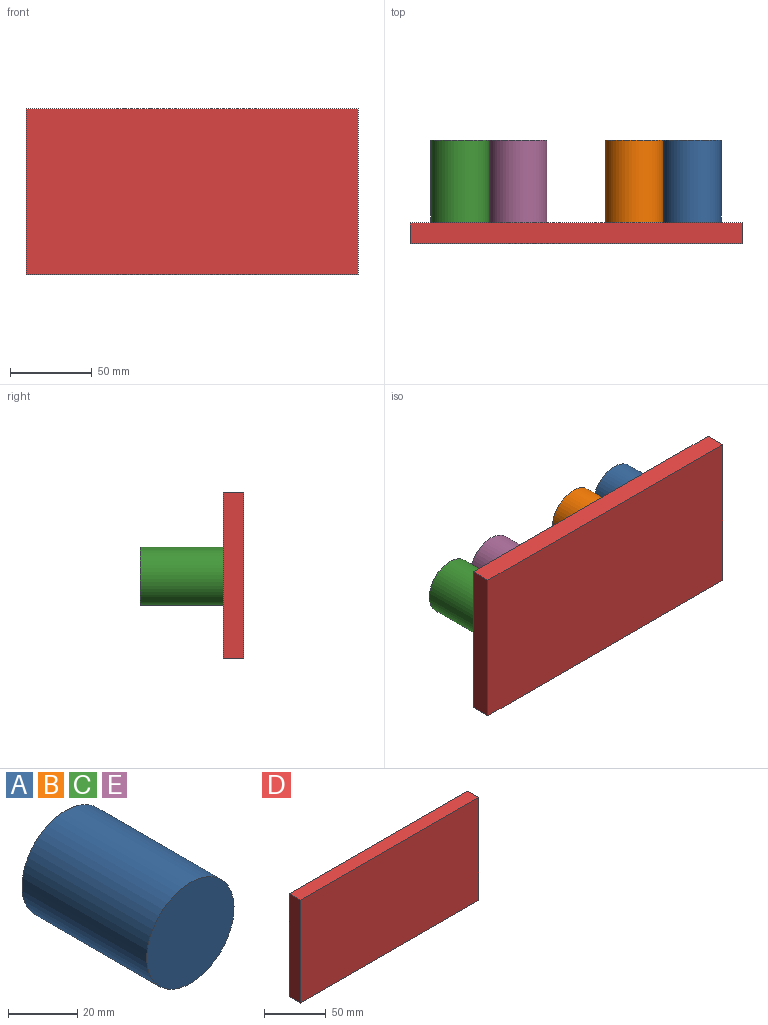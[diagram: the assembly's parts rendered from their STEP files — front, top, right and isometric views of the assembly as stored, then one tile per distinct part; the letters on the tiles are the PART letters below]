
ASSEMBLY  parts=5 mates=4
PART A: 3 faces, bbox 35.6x50.8x35.6 mm
  f0: cylinder r=17.78mm len=50.8mm, axis (0,1,0), area 5675.1mm2, adj f1,f2
  f1: plane 35.56x35.56mm, normal (0,-1,0), area 993.1mm2, adj f0
  f2: plane 35.56x35.56mm, normal (0,1,0), area 993.1mm2, adj f0
PART B: same geometry as A
PART C: same geometry as A
PART D: 6 faces, bbox 203.2x12.7x101.6 mm
  f0: plane 203.2x12.7mm, normal (0,0,-1), area 2580.6mm2, adj f1,f3,f4,f5
  f1: plane 101.6x12.7mm, normal (1,0,0), area 1290.3mm2, adj f0,f2,f4,f5
  f2: plane 203.2x12.7mm, normal (0,0,1), area 2580.6mm2, adj f1,f3,f4,f5
  f3: plane 101.6x12.7mm, normal (-1,0,0), area 1290.3mm2, adj f0,f2,f4,f5
  f4: plane 203.2x101.6mm, normal (0,-1,0), area 20645.1mm2, adj f0,f1,f2,f3
  f5: plane 203.2x101.6mm, normal (0,1,0), area 20645.1mm2, adj f0,f1,f2,f3
PART E: same geometry as A
PLACE A t=(123.38,81.38,77.98)mm
PLACE B t=(87.82,81.38,77.98)mm
PLACE C t=(-18.86,81.38,77.98)mm
PLACE D t=(52.26,30.58,77.98)mm
PLACE E t=(16.7,81.38,77.98)mm
MATE fastened E.f0 <-> D.f5  axis (0,1,0) through (16.7,30.58,77.98)mm
MATE fastened B.f0 <-> D.f5  axis (0,1,0) through (87.82,30.58,77.98)mm
MATE fastened C.f0 <-> D.f5  axis (0,-1,0) through (-18.86,30.58,77.98)mm
MATE fastened A.f0 <-> D.f5  axis (0,1,0) through (123.38,30.58,77.98)mm
